# Revit family: Haworth_ComposeBeam_Panel_Solid
name_source: partatom
category: Furniture Systems
revit_build: Autodesk Revit 2018 (Build: 20170223_1515(x64)
units: mm (PartAtom-declared; Revit-internal decimal feet)

## family parameters
Always vertical = Yes
Cut with Voids When Loaded = No
OmniClass Number = 23.40.70.14.64.21
OmniClass Title = Systems Furniture
Part Type = Normal
Room Calculation Point = No
Round Connector Dimension = Use Diameter
Shared = No
Work Plane-Based = No

## types (1)
- 72w 25h
    Actual Height = 25 1/2"
    Actual Width = 72"
    Assembly Code = E2020500
    Bottom Trim Width = 1 1/2"
    Custom Size = No
    Description = Haworth - Compose Connections - Panel - Solid
    Gap Offset = 1/4"
    Height = 25 1/2"
    Manufacturer = Haworth
    Max. Width = 72"
    Min. Width = 24"
    Min/Max Height = 25.5 in.
    Min/Max Width = 24-72 in. @ 6 in. Increments
    Model = VZFS
    Panel Depth = 1/2"
    Panel Width = 72"
    Revision Number = 3
    Size = Verify Final Dim. w/ Haworth
    Sustainability Info = http://media.haworth.com
    Technology Trim Finish = Haworth _ Paint _ Gray Tone
    Top Trim Width = 1/4"
    Trim Depth = 3"
    Trim Finish = Haworth _ Paint _ Gray Tone
    URL = http://www.haworth.com
    URL - Product = http://haworth.com
    Warranty = https://www.haworth.com
    Width = 72"

## geometry (parser evidence)
native form markers: Sweep x4
no freeform markers — native parametric forms only
